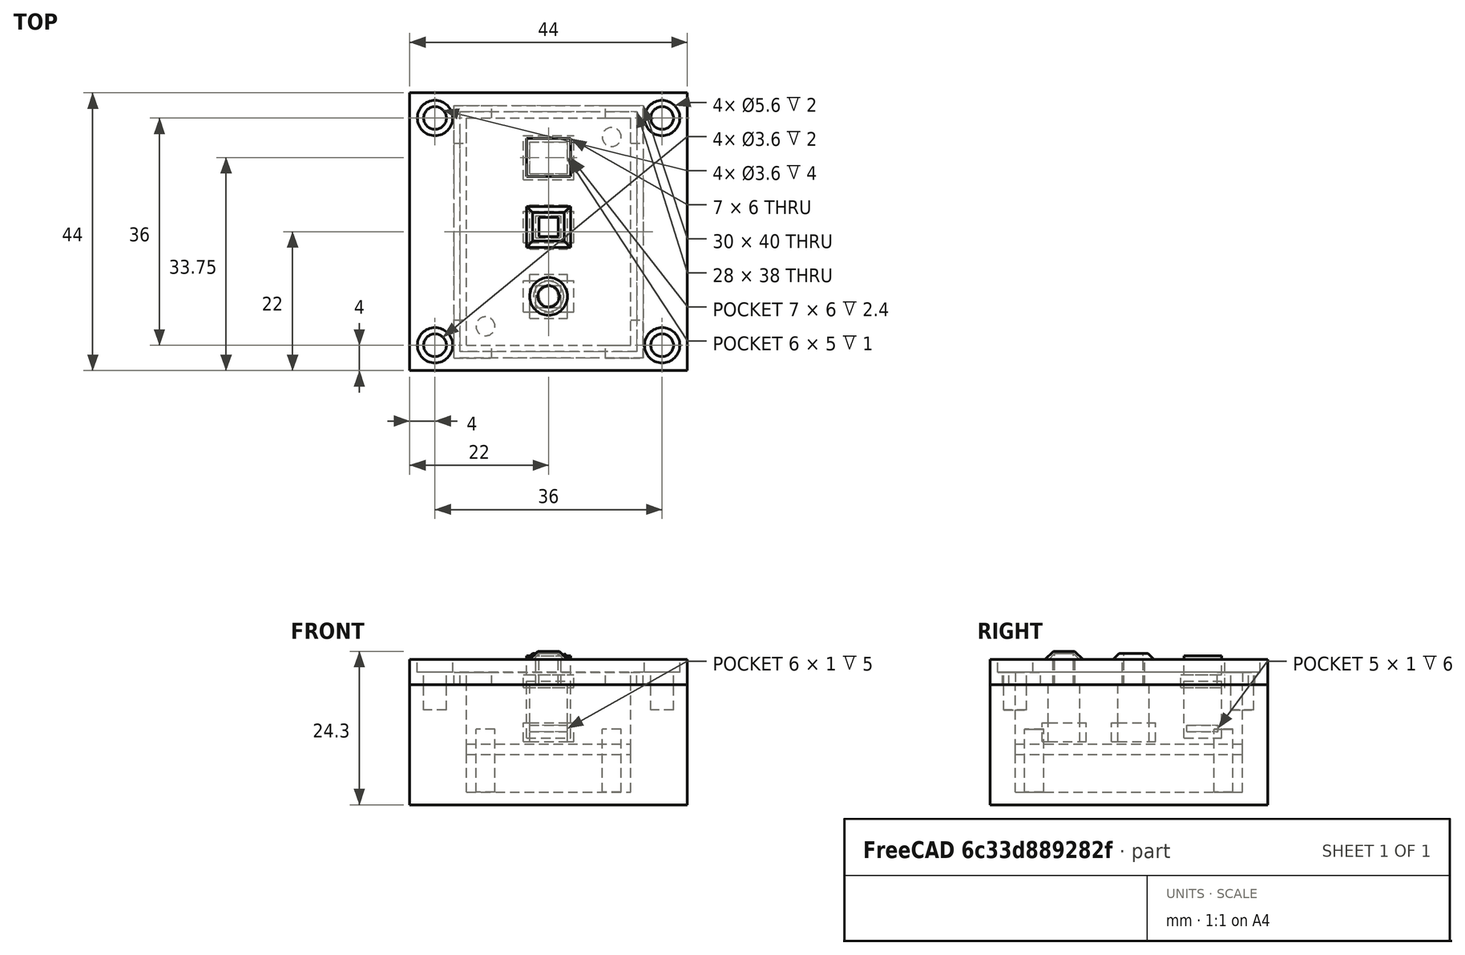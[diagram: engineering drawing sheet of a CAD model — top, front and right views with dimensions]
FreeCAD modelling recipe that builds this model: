
FCSTD DOCUMENT  (FreeCAD 0.15R4671 (Git))
Label: Button_V03
License: All rights reserved
LicenseURL: http://en.wikipedia.org/wiki/All_rights_reserved
objects: Part::Box×41, Part::Cylinder×15, Part::MultiFuse×15, Part::Cut×8, Mesh::Feature×7, Part::Cone×2, Sketcher::SketchObject×2, PartDesign::Pad×2, Part::Chamfer×1
note: 88 computed .brp shape members not serialized (recipe doc carries the construction recipe); baked Part::Feature solids carry a one-line shape summary decoded from their .brp

FEATURE [Part::Box] Box  label="Box_out"
  Height = 19
  Length = 44
  Placement = pos=(-7,-2,0) rot=(0,0,1;0rad)
  Width = 44
FEATURE [Part::Box] Box001  label="Box_in"
  Height = 17
  Length = 26
  Placement = pos=(2,2,2) rot=(0,0,1;0rad)
  Width = 36
FEATURE [Part::Cut] Cut  label="BoX_base"
  Base = -> Box
  Tool = -> Box001
FEATURE [Part::Box] Box002  label="PCB"
  Height = 1.6
  Length = 26
  Placement = pos=(2,2,8) rot=(0,0,1;0rad)
  Width = 36
FEATURE [Part::Box] Box003  label="Button1_001"
  Height = 6
  Length = 6
  Placement = pos=(12,7.25,9) rot=(0,0,1;0rad)
  Width = 5
FEATURE [Part::Box] Box004  label="Button1_002"
  Height = 3
  Length = 1
  Placement = pos=(11,7.25,6) rot=(0,0,1;0rad)
  Width = 5
FEATURE [Part::Box] Box005  label="Button1_003"
  Height = 3
  Length = 1
  Placement = pos=(18,7.25,6) rot=(0,0,1;0rad)
  Width = 5
FEATURE [Part::Box] Box006  label="Button1_004"
  Height = 3
  Length = 6
  Placement = pos=(12,6.25,6) rot=(0,0,1;0rad)
  Width = 1
FEATURE [Part::Box] Box007  label="Button1_005"
  Height = 3
  Length = 6
  Placement = pos=(12,12.25,6) rot=(0,0,1;0rad)
  Width = 1
FEATURE [Part::Cylinder] Cylinder  label="Button1_006"
  Angle = 360
  Height = 10
  Placement = pos=(15,9.75,10) rot=(0,0,1;0rad)
  Radius = 1.5
FEATURE [Part::Box] Box014  label="Button1_box0001"
  Height = 4
  Length = 4
  Placement = pos=(13,8,19) rot=(0,0,1;0rad)
  Width = 3.5
FEATURE [Part::Box] Box015  label="Button2_box0001"
  Height = 4
  Length = 4
  Placement = pos=(13,19,19) rot=(0,0,1;0rad)
  Width = 3.5
FEATURE [Part::MultiFuse] Fusion004  label="Fusion004_cut"
  Shapes = -> [Box015,Box014]
FEATURE [Mesh::Feature] Button
  Placement = pos=(15,36,8) rot=(1,0,0;1.5708rad)
FEATURE [Mesh::Feature] Button001
  Placement = pos=(15,47,8) rot=(1,0,0;1.5708rad)
FEATURE [Part::Box] Box036  label="Button2_006"
  Height = 10
  Length = 3
  Placement = pos=(13.5,8.25,10) rot=(0,0,1;0rad)
  Width = 3
FEATURE [Part::Box] Box037  label="Button1_007"
  Height = 6
  Length = 6
  Placement = pos=(12,7.25,9) rot=(0,0,1;0rad)
  Width = 5
FEATURE [Part::Box] Box038  label="Button1_008"
  Height = 3
  Length = 1
  Placement = pos=(11,7.25,6) rot=(0,0,1;0rad)
  Width = 5
FEATURE [Part::Box] Box039  label="Button1_009"
  Height = 3
  Length = 1
  Placement = pos=(18,7.25,6) rot=(0,0,1;0rad)
  Width = 5
FEATURE [Part::Box] Box040  label="Button1_010"
  Height = 3
  Length = 6
  Placement = pos=(12,6.25,6) rot=(0,0,1;0rad)
  Width = 1
FEATURE [Part::Box] Box041  label="Button1_011"
  Height = 3
  Length = 6
  Placement = pos=(12,12.25,6) rot=(0,0,1;0rad)
  Width = 1
FEATURE [Part::MultiFuse] Fusion010  label="Button_Extender002"
  Shapes = -> [Box037,Box038,Box039,Box040,Box041]
FEATURE [Part::MultiFuse] Fusion011  label="Bt_Ex2"
  Placement = pos=(0,11,4) rot=(0,0,1;0rad)
  Shapes = -> [Fusion010,Box036]
FEATURE [Part::Cylinder] Cylinder001  label="MtH001"
  Angle = 360
  Height = 10
  Placement = pos=(5,5,2) rot=(0,0,1;0rad)
  Radius = 1.5
FEATURE [Part::Cylinder] Cylinder002  label="MtH002"
  Angle = 360
  Height = 10
  Placement = pos=(25,35,2) rot=(0,0,1;0rad)
  Radius = 1.5
FEATURE [Part::Box] Box042  label="Box_top"
  Height = 4
  Length = 44
  Placement = pos=(-7,-2,19) rot=(0,0,1;0rad)
  Width = 44
FEATURE [Mesh::Feature] Button002
  Placement = pos=(15,58,8) rot=(1,0,0;1.5708rad)
FEATURE [Part::Box] Box043  label="Cube"
  Height = 2
  Length = 2
  Placement = pos=(0,0,19) rot=(0,0,1;0rad)
  Width = 6
FEATURE [Part::Box] Box044  label="Cube001"
  Height = 2
  Length = 6
  Placement = pos=(0,0,19) rot=(0,0,1;0rad)
  Width = 2
FEATURE [Part::Box] Box045  label="Cube002"
  Height = 2
  Length = 6
  Placement = pos=(24,0,19) rot=(0,0,1;0rad)
  Width = 2
FEATURE [Part::Box] Box046  label="Cube003"
  Height = 2
  Length = 6
  Placement = pos=(0,38,19) rot=(0,0,1;0rad)
  Width = 2
FEATURE [Part::Box] Box048  label="Cube005"
  Height = 2
  Length = 6
  Placement = pos=(24,38,19) rot=(0,0,1;0rad)
  Width = 2
FEATURE [Part::Box] Box049  label="Cube006"
  Height = 2
  Length = 2
  Placement = pos=(28,0,19) rot=(0,0,1;0rad)
  Width = 6
FEATURE [Part::Box] Box050  label="Cube007"
  Height = 2
  Length = 2
  Placement = pos=(0,34,19) rot=(0,0,1;0rad)
  Width = 6
FEATURE [Part::Box] Box051  label="Cube008"
  Height = 2
  Length = 2
  Placement = pos=(28,34,19) rot=(0,0,1;0rad)
  Width = 6
FEATURE [Part::MultiFuse] Fusion012  label="Support"
  Shapes = -> [Box043,Box044,Box045,Box046,Box048,Box049,Box050,Box051]
FEATURE [Part::Box] Box052  label="Cube009"
  Height = 2
  Length = 2
  Placement = pos=(0,0,19) rot=(0,0,1;0rad)
  Width = 6
FEATURE [Part::Box] Box053  label="Cube010"
  Height = 2
  Length = 6
  Placement = pos=(0,0,19) rot=(0,0,1;0rad)
  Width = 2
FEATURE [Part::Box] Box054  label="Cube011"
  Height = 2
  Length = 6
  Placement = pos=(24,0,19) rot=(0,0,1;0rad)
  Width = 2
FEATURE [Part::Box] Box055  label="Cube012"
  Height = 2
  Length = 6
  Placement = pos=(0,38,19) rot=(0,0,1;0rad)
  Width = 2
FEATURE [Part::Box] Box056  label="Cube013"
  Height = 2
  Length = 6
  Placement = pos=(24,38,19) rot=(0,0,1;0rad)
  Width = 2
FEATURE [Part::Box] Box057  label="Cube014"
  Height = 2
  Length = 2
  Placement = pos=(28,0,19) rot=(0,0,1;0rad)
  Width = 6
FEATURE [Part::Box] Box058  label="Cube015"
  Height = 2
  Length = 2
  Placement = pos=(0,34,19) rot=(0,0,1;0rad)
  Width = 6
FEATURE [Part::Box] Box059  label="Cube016"
  Height = 2
  Length = 2
  Placement = pos=(28,34,19) rot=(0,0,1;0rad)
  Width = 6
FEATURE [Part::MultiFuse] Fusion013  label="Support_cut"
  Shapes = -> [Box052,Box053,Box054,Box055,Box056,Box057,Box058,Box059]
FEATURE [Part::Box] Box060  label="Button1_012"
  Height = 1
  Length = 6
  Placement = pos=(12,29.18,11.6) rot=(0,0,1;0rad)
  Width = 5
FEATURE [Part::Box] Box065  label="Button1_box0002"
  Height = 3
  Length = 7
  Placement = pos=(11.5,17.5,21) rot=(0,0,1;0rad)
  Width = 6.5
FEATURE [Part::Cone] Cone
  Angle = 360
  Height = 1.3
  Placement = pos=(15,9.75,21) rot=(0,0,1;0rad)
  Radius1 = 3
  Radius2 = 1.7
FEATURE [Part::Cone] Cone001
  Angle = 360
  Height = 1
  Placement = pos=(15,9.75,21) rot=(0,0,1;0rad)
  Radius1 = 2.4
  Radius2 = 1.5
FEATURE [Part::Cut] Cut003  label="Button_Top_cover001"
  Base = -> Cone
  Placement = pos=(0,0,2) rot=(0,0,1;0rad)
  Tool = -> Cone001
FEATURE [Mesh::Feature] M3x6mm_Screw
  Placement = pos=(-3,38,15) rot=(0,0,1;0rad)
FEATURE [Mesh::Feature] M3x6mm_Screw001
  Placement = pos=(-3,2,15) rot=(0,0,1;0rad)
FEATURE [Mesh::Feature] M3x6mm_Screw002
  Placement = pos=(33,38,15) rot=(0,0,1;0rad)
FEATURE [Mesh::Feature] M3x6mm_Screw003
  Placement = pos=(33,2,15) rot=(0,0,1;0rad)
FEATURE [Sketcher::SketchObject] Sketch
  Placement = pos=(2,2,19) rot=(0,0,1;0rad)
  sketch-geometry (8):
    g0: LineSegment StartX=-1 StartY=37 StartZ=0 EndX=27 EndY=37 EndZ=0
    g1: LineSegment StartX=27 StartY=37 StartZ=0 EndX=27 EndY=-1 EndZ=0
    g2: LineSegment StartX=27 StartY=-1 StartZ=0 EndX=-1 EndY=-1 EndZ=0
    g3: LineSegment StartX=-1 StartY=-1 StartZ=0 EndX=-1 EndY=37 EndZ=0
    g4: LineSegment StartX=-2 StartY=38 StartZ=0 EndX=28 EndY=38 EndZ=0
    g5: LineSegment StartX=28 StartY=38 StartZ=0 EndX=28 EndY=-2 EndZ=0
    g6: LineSegment StartX=28 StartY=-2 StartZ=0 EndX=-2 EndY=-2 EndZ=0
    g7: LineSegment StartX=-2 StartY=-2 StartZ=0 EndX=-2 EndY=38 EndZ=0
  constraints (24):
    c: Coincident(g0,g1)
    c: Coincident(g1,g2)
    c: Coincident(g2,g3)
    c: Coincident(g3,g0)
    c: Horizontal(g0)
    c: Horizontal(g2)
    c: Vertical(g1)
    c: Vertical(g3)
    c: DistanceY(g-1,g1) = -1
    c: DistanceY(g-1,g0) = 37
    c: DistanceX(g-1,g2) = -1
    c: DistanceX(g-1,g1) = 27
    c: Coincident(g4,g5)
    c: Coincident(g5,g6)
    c: Coincident(g6,g7)
    c: Coincident(g7,g4)
    c: Horizontal(g4)
    c: Horizontal(g6)
    c: Vertical(g5)
    c: Vertical(g7)
    c: DistanceY(g6,g2) = 1
    c: DistanceX(g6,g2) = 1
    c: DistanceY(g4,g0) = -1
    c: DistanceX(g1,g5) = 1
FEATURE [PartDesign::Pad] Pad  label="Gasket_add"
  Length = 2
  Length2 = 100
  Placement = pos=(2,2,19) rot=(0,0,1;0rad)
  Sketch = -> Sketch
  Type = 0
FEATURE [Sketcher::SketchObject] Sketch001
  Placement = pos=(2,2,19) rot=(0,0,1;0rad)
  sketch-geometry (8):
    g0: LineSegment StartX=-1 StartY=37 StartZ=0 EndX=27 EndY=37 EndZ=0
    g1: LineSegment StartX=27 StartY=37 StartZ=0 EndX=27 EndY=-1 EndZ=0
    g2: LineSegment StartX=27 StartY=-1 StartZ=0 EndX=-1 EndY=-1 EndZ=0
    g3: LineSegment StartX=-1 StartY=-1 StartZ=0 EndX=-1 EndY=37 EndZ=0
    g4: LineSegment StartX=-2 StartY=38 StartZ=0 EndX=28 EndY=38 EndZ=0
    g5: LineSegment StartX=28 StartY=38 StartZ=0 EndX=28 EndY=-2 EndZ=0
    g6: LineSegment StartX=28 StartY=-2 StartZ=0 EndX=-2 EndY=-2 EndZ=0
    g7: LineSegment StartX=-2 StartY=-2 StartZ=0 EndX=-2 EndY=38 EndZ=0
  constraints (24):
    c: Coincident(g0,g1)
    c: Coincident(g1,g2)
    c: Coincident(g2,g3)
    c: Coincident(g3,g0)
    c: Horizontal(g0)
    c: Horizontal(g2)
    c: Vertical(g1)
    c: Vertical(g3)
    c: DistanceY(g-1,g1) = -1
    c: DistanceY(g-1,g0) = 37
    c: DistanceX(g-1,g2) = -1
    c: DistanceX(g-1,g1) = 27
    c: Coincident(g4,g5)
    c: Coincident(g5,g6)
    c: Coincident(g6,g7)
    c: Coincident(g7,g4)
    c: Horizontal(g4)
    c: Horizontal(g6)
    c: Vertical(g5)
    c: Vertical(g7)
    c: DistanceY(g6,g2) = 1
    c: DistanceX(g6,g2) = 1
    c: DistanceY(g4,g0) = -1
    c: DistanceX(g1,g5) = 1
FEATURE [PartDesign::Pad] Pad001  label="Gasket_cut"
  Length = 2
  Length2 = 100
  Placement = pos=(2,2,19) rot=(0,0,1;0rad)
  Sketch = -> Sketch001
  Type = 0
FEATURE [Part::Cylinder] Cylinder005  label="MH_Cut001"
  Angle = 360
  Height = 6
  Placement = pos=(-3,2,15) rot=(0,0,1;0rad)
  Radius = 1.8
FEATURE [Part::Cylinder] Cylinder006  label="MH_Cut002"
  Angle = 360
  Height = 6
  Placement = pos=(-3,38,15) rot=(0,0,1;0rad)
  Radius = 1.8
FEATURE [Part::Cylinder] Cylinder007  label="MH_Cut003"
  Angle = 360
  Height = 6
  Placement = pos=(33,2,15) rot=(0,0,1;0rad)
  Radius = 1.8
FEATURE [Part::Cylinder] Cylinder008  label="MH_Cut004"
  Angle = 360
  Height = 6
  Placement = pos=(33,38,15) rot=(0,0,1;0rad)
  Radius = 1.8
FEATURE [Part::MultiFuse] Fusion017  label="Screw_cut001"
  Shapes = -> [Cylinder005,Cylinder006,Cylinder007,Cylinder008]
FEATURE [Part::Cylinder] Cylinder009  label="MH_Cut005"
  Angle = 360
  Height = 6
  Placement = pos=(-3,2,15) rot=(0,0,1;0rad)
  Radius = 1.8
FEATURE [Part::Cylinder] Cylinder010  label="MH_Cut006"
  Angle = 360
  Height = 6
  Placement = pos=(-3,38,15) rot=(0,0,1;0rad)
  Radius = 1.8
FEATURE [Part::Cylinder] Cylinder011  label="MH_Cut007"
  Angle = 360
  Height = 6
  Placement = pos=(33,2,15) rot=(0,0,1;0rad)
  Radius = 1.8
FEATURE [Part::Cylinder] Cylinder012  label="MH_Cut008"
  Angle = 360
  Height = 6
  Placement = pos=(33,38,15) rot=(0,0,1;0rad)
  Radius = 1.8
FEATURE [Part::MultiFuse] Fusion018  label="Screw_cut002"
  Shapes = -> [Cylinder009,Cylinder010,Cylinder011,Cylinder012]
FEATURE [Part::Cylinder] Cylinder013  label="Screw_head001"
  Angle = 360
  Height = 3
  Placement = pos=(-3,2,21) rot=(0,0,1;0rad)
  Radius = 2.8
FEATURE [Part::Cylinder] Cylinder014  label="Screw_head002"
  Angle = 360
  Height = 3
  Placement = pos=(-3,38,21) rot=(0,0,1;0rad)
  Radius = 2.8
FEATURE [Part::Cylinder] Cylinder015  label="Screw_head003"
  Angle = 360
  Height = 3
  Placement = pos=(33,38,21) rot=(0,0,1;0rad)
  Radius = 2.8
FEATURE [Part::Cylinder] Cylinder016  label="Screw_head004"
  Angle = 360
  Height = 3
  Placement = pos=(33,2,21) rot=(0,0,1;0rad)
  Radius = 2.8
FEATURE [Part::MultiFuse] Fusion019  label="Screw_Head_cut"
  Shapes = -> [Cylinder016,Cylinder015,Cylinder014,Cylinder013]
FEATURE [Part::Chamfer] Chamfer  label="Button_Top_cover002"
  Base = -> Box065
  Edges = 4 edges r=0.99: [Edge2,Edge6,Edge10,Edge12]
FEATURE [Part::MultiFuse] Fusion020  label="top_cut"
  Shapes = -> [Fusion018,Pad001,Fusion019,Fusion004]
FEATURE [Part::Cut] Cut004
  Base = -> Box042
  Tool = -> Fusion020
FEATURE [Part::Box] Box069  label="Button2_box0002"
  Height = 4
  Length = 4
  Placement = pos=(13,19,19) rot=(0,0,1;0rad)
  Width = 3.5
FEATURE [Part::Cut] Cut006  label="Button_Top_cover002_1"
  Base = -> Chamfer
  Tool = -> Box069
FEATURE [Part::MultiFuse] Fusion022
  Shapes = -> [Pad,Cylinder002,Cylinder001]
FEATURE [Part::Cut] Cut007
  Base = -> Cut
  Tool = -> Fusion017
FEATURE [Part::MultiFuse] Fusion023  label="Base_final"
  Shapes = -> [Cut007,Fusion022]
FEATURE [Part::MultiFuse] Fusion  label="Button_Extender001"
  Shapes = -> [Box003,Box004,Box005,Box006,Box007]
FEATURE [Part::MultiFuse] Fusion005  label="Bt_Ex1"
  Placement = pos=(0,0,4) rot=(0,0,1;0rad)
  Shapes = -> [Fusion,Cylinder]
FEATURE [Part::Box] Box070  label="Button1_013"
  Height = 9
  Length = 7
  Placement = pos=(11.5,28.75,10.6) rot=(0,0,1;0rad)
  Width = 6
FEATURE [Part::Cut] Cut008  label="Bt_Ex3.1"
  Base = -> Box070
  Tool = -> Box060
FEATURE [Part::Box] Box071  label="Button1_014"
  Height = 3
  Length = 7
  Placement = pos=(11.5,28.75,20.6) rot=(0,0,1;0rad)
  Width = 6
FEATURE [Part::Box] Box072  label="Button1_015"
  Height = 2
  Length = 8
  Placement = pos=(11,28.25,18.6) rot=(0,0,1;0rad)
  Width = 7
FEATURE [Part::Box] Box073  label="Button1_016"
  Height = 1
  Length = 7
  Placement = pos=(11.5,28.75,18.6) rot=(0,0,1;0rad)
  Width = 6
FEATURE [Part::MultiFuse] Fusion024
  Shapes = -> [Box071,Box072]
FEATURE [Part::Cut] Cut009  label="Bt_Ex3.2"
  Base = -> Fusion024
  Tool = -> Box073
FEATURE [Part::Box] Box074  label="Button1_017"
  Height = 3
  Length = 7
  Placement = pos=(11.5,28.75,20.6) rot=(0,0,1;0rad)
  Width = 6
FEATURE [Part::Cut] Cut010  label="Top__"
  Base = -> Cut004
  Tool = -> Box074
FEATURE [Part::MultiFuse] Fusion025  label="Top_final"
  Shapes = -> [Cut010,Cut006,Cut003]
